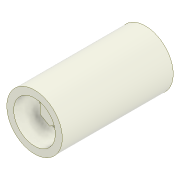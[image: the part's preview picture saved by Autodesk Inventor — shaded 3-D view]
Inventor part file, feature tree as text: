
AUTODESK INVENTOR PART (.ipt)
format: ipt  version: 2022 (Build 260153000, 153)  size: 171,520 bytes
history: native  units: mm
features: sketch x6, thicken_offset x5, extrude x3, hole x3, chamfer x1
ambient origin geometry x8: Origin, YZ Plane, XZ Plane, XY Plane, X Axis, Y Axis, Z Axis, Center Point
bodies: Solid1 (feature_tree)
feature tree (18):
  extrude  "Adapter"  Depth=9.0mm TaperAngle=0.0deg
  hole  "Hole1"  [1 undecoded]
  hole  "Hole2"  [1 undecoded]
  extrude  "Driver Gear Profile"  Depth=0.13mm
  extrude  "Motor Shaft Profile"  Depth=6.0mm
  chamfer  "Chamfer1"  Distance=5.5mm
  thicken_offset  "Thicken1"
  thicken_offset  "Thicken2"
  thicken_offset  "Thicken3"
  thicken_offset  "Thicken5"
  thicken_offset  "Thicken6"
  hole  "Hole6"  [1 undecoded]
  sketch  "Sketch1"  dims[d1=11.0mm d2=9.0mm d3=0.0mm]
  sketch  "Sketch2"  dims[d4=13.0mm d5=0.0mm]
  sketch  "Sketch3"  dims[d6=8.0mm d7=6.0mm d8=4.0mm d9=2.0mm d10=90.0deg d11=5.0mm d12=0.0mm]
  sketch  "Sketch4"  dims[d13=6.3mm d14=6.0mm d15=4.0mm d16=2.0mm d17=90.0deg d18=4.0mm d19=0.0mm d20=4.0mm]
  sketch  "Sketch6"  dims[d21=6.0mm d22=0.0mm d27=0.1mm d28=0.15mm]
  sketch  "Sketch9"  dims[d29=0.15mm d30=0.15mm d31=0.13mm d32=0.15mm d35=6.0mm d36=5.5mm d37=12.0mm d38=0.0mm d39=0.2mm d40=0.1mm d48=0.5mm d49=2.0mm d50=45.0deg d58=0.2mm d59=0.2mm d67=2.85mm d68=7.0mm d69=4.0mm d70=2.0mm d71=90.0deg d72=10.4mm d73=20.594885mm d41=1.0mm d42=1.0mm d43=1.0mm d44=0.15mm d45=0.25mm d46=0.375mm d47=14.3117mm d51=0.75mm d52=0.375mm d60=0.5mm d61=0.872665mm]
note: 3 required parameter values undecoded (feature->parameter linkage not recoverable at this tier; creation-order binding heuristic only, values carry confidence <= 0.55)
